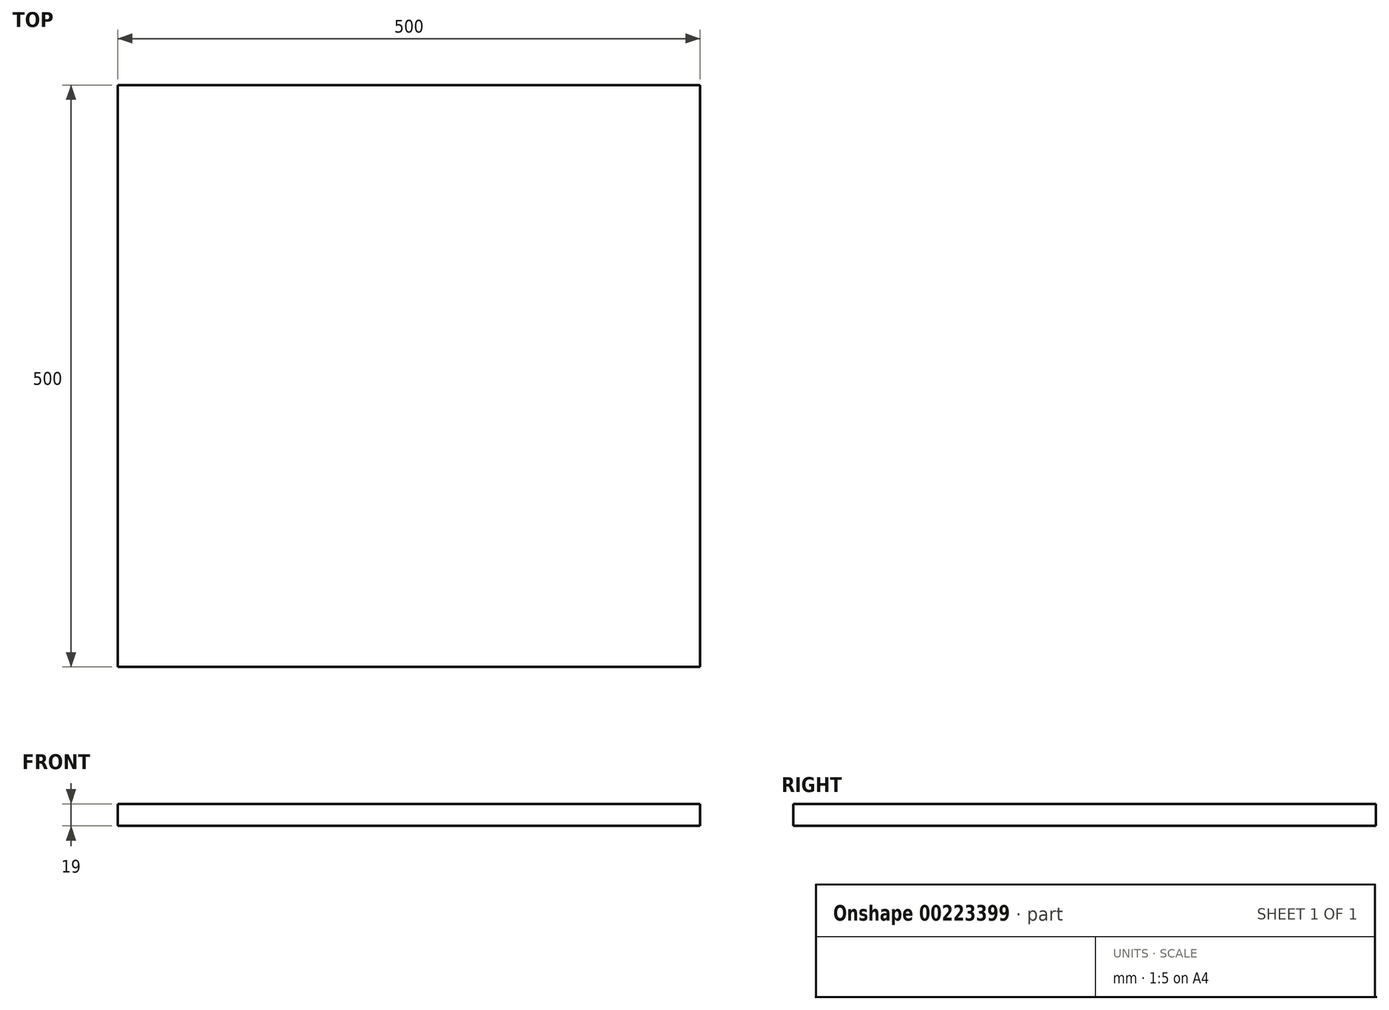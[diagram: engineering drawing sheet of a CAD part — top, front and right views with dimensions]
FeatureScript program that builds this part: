
annotation { "Feature Type Name" : "Feature", "Feature Type Description" : "" }
export const myFeature = defineFeature(function(context is Context, id is Id, definition is map)
    precondition{}
    {
        {
            var Q0;
            Q0=qCreatedBy(makeId("Top.planeOp"),FACE);
            var sketch = newSketch(context, id + "F0", { "sketchPlane" : qUnion([Q0])});
            skLineSegment(sketch, "E0.bottom", {"start": v(40.77, 13.84) * mm, "end": v(540.77, 13.84) * mm});
            skLineSegment(sketch, "E0.top", {"start": v(40.77, 513.84) * mm, "end": v(540.77, 513.84) * mm});
            skLineSegment(sketch, "E0.left", {"start": v(40.77, 13.84) * mm, "end": v(40.77, 513.84) * mm});
            skLineSegment(sketch, "E0.right", {"start": v(540.77, 13.84) * mm, "end": v(540.77, 513.84) * mm});
            skSolve(sketch);
        }
        {
            var Q0;
            Q0=makeQuery(id+"F0.imprint","IMPRINT",FACE,{"disambiguationData":[TD([[makeQuery(id+"F0.imprint","IMPRINT",EDGE,{"derivedFrom":sQuery(id+"F0.wireOp",EDGE,"E0.bottom")}),1.0]])]});
            extrude(context, id + "F1", {"entities" : qUnion([Q0]), "depth" : 19 * mm});
        }
    });
